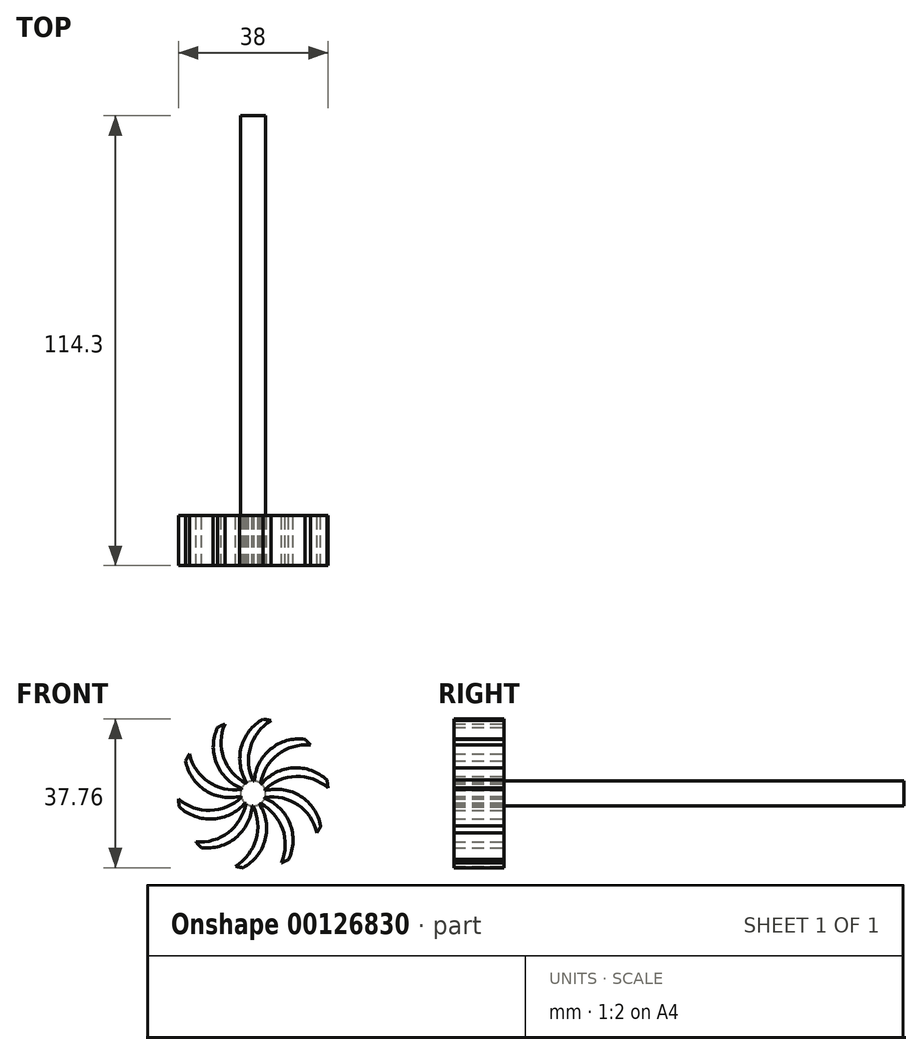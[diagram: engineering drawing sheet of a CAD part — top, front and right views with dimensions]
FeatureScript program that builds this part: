
annotation { "Feature Type Name" : "Feature", "Feature Type Description" : "" }
export const myFeature = defineFeature(function(context is Context, id is Id, definition is map)
    precondition{}
    {
        {
            var Q0;
            Q0=qCreatedBy(makeId("Front.planeOp"),FACE);
            var sketch = newSketch(context, id + "F0", { "sketchPlane" : qUnion([Q0])});
            skCircle(sketch, "E0", {"center": v(0, 0) * mm, "radius": 3.18 * mm});
            skSolve(sketch);
        }
        {
            var Q0;
            Q0=makeQuery(id+"F0.imprint","IMPRINT",FACE,{"disambiguationData":[TD([[makeQuery(id+"F0.imprint","IMPRINT",EDGE,{"derivedFrom":sQuery(id+"F0.wireOp",EDGE,"E0")}),1.0]])]});
            extrude(context, id + "F1", {"entities" : qUnion([Q0]), "depth" : 101.6 * mm});
        }
        {
            var Q0;
            Q0=makeQuery(id+"F1.opExtrude","CAP_FACE",FACE,{"disambiguationData":[OSD([sQuery(id+"F0.wireOp",EDGE,"E0")])],"isStart":false});
            var sketch = newSketch(context, id + "F2", { "sketchPlane" : qUnion([Q0])});
            skCircle(sketch, "E1", {"center": v(0, 0) * mm, "radius": 19.05 * mm});
            skArc(sketch, "E2", {"start": v(4.53, 18.5) * mm, "mid": v(-0.72, 11.72) * mm, "end": v(0, 3.18) * mm});
            skArc(sketch, "E3", {"start": v(2.56, 18.88) * mm, "mid": v(-3.04, 11.7) * mm, "end": v(-1.63, 2.72) * mm});
            skArc(sketch, "E4.1.0", {"start": v(-9.03, 16.77) * mm, "mid": v(-9.34, 7.69) * mm, "end": v(-2.92, 1.24) * mm});
            skArc(sketch, "E4.1.1", {"start": v(-7.2, 17.63) * mm, "mid": v(-7.47, 9.06) * mm, "end": v(-1.87, 2.57) * mm});
            skArc(sketch, "E4.2.0", {"start": v(-17.16, 8.26) * mm, "mid": v(-12.07, 0.73) * mm, "end": v(-3.1, -0.71) * mm});
            skArc(sketch, "E4.2.1", {"start": v(-16.2, 10.03) * mm, "mid": v(-11.37, 2.94) * mm, "end": v(-3.02, 0.98) * mm});
            skArc(sketch, "E4.3.0", {"start": v(-18.74, -3.4) * mm, "mid": v(-10.2, -6.5) * mm, "end": v(-2.09, -2.4) * mm});
            skArc(sketch, "E4.3.1", {"start": v(-19, -1.4) * mm, "mid": v(-10.93, -4.3) * mm, "end": v(-3.02, -0.98) * mm});
            skArc(sketch, "E4.4.0", {"start": v(-13.16, -13.77) * mm, "mid": v(-4.43, -11.26) * mm, "end": v(-0.28, -3.16) * mm});
            skArc(sketch, "E4.4.1", {"start": v(-14.54, -12.3) * mm, "mid": v(-6.3, -9.9) * mm, "end": v(-1.87, -2.57) * mm});
            skArc(sketch, "E4.5.0", {"start": v(-2.56, -18.88) * mm, "mid": v(3.04, -11.7) * mm, "end": v(1.63, -2.72) * mm});
            skArc(sketch, "E4.5.1", {"start": v(-4.53, -18.5) * mm, "mid": v(0.72, -11.72) * mm, "end": v(0, -3.17) * mm});
            skArc(sketch, "E4.6.0", {"start": v(9.03, -16.77) * mm, "mid": v(9.34, -7.69) * mm, "end": v(2.92, -1.24) * mm});
            skArc(sketch, "E4.6.1", {"start": v(7.2, -17.63) * mm, "mid": v(7.47, -9.06) * mm, "end": v(1.87, -2.57) * mm});
            skArc(sketch, "E4.7.0", {"start": v(17.16, -8.26) * mm, "mid": v(12.07, -0.73) * mm, "end": v(3.1, 0.71) * mm});
            skArc(sketch, "E4.7.1", {"start": v(16.2, -10.03) * mm, "mid": v(11.37, -2.94) * mm, "end": v(3.02, -0.98) * mm});
            skArc(sketch, "E4.8.0", {"start": v(18.74, 3.4) * mm, "mid": v(10.2, 6.5) * mm, "end": v(2.09, 2.4) * mm});
            skArc(sketch, "E4.8.1", {"start": v(19, 1.4) * mm, "mid": v(10.93, 4.3) * mm, "end": v(3.02, 0.98) * mm});
            skArc(sketch, "E4.9.0", {"start": v(13.16, 13.77) * mm, "mid": v(4.43, 11.26) * mm, "end": v(0.28, 3.16) * mm});
            skArc(sketch, "E4.9.1", {"start": v(14.54, 12.3) * mm, "mid": v(6.3, 9.9) * mm, "end": v(1.87, 2.57) * mm});
            skSolve(sketch);
        }
        {
            var Q0;
            {var subQ0=sQuery(id+"F2.wireOp",EDGE,"E2");Q0=makeQuery(id+"F2.imprint","IMPRINT",FACE,{"disambiguationData":[TD([[makeQuery(id+"F2.imprint","IMPRINT",EDGE,{"derivedFrom":subQ0}),-1.0]])]});}
            var Q1;
            {var subQ0=sQuery(id+"F2.wireOp",EDGE,"E4.9.0");Q1=makeQuery(id+"F2.imprint","IMPRINT",FACE,{"disambiguationData":[TD([[makeQuery(id+"F2.imprint","IMPRINT",EDGE,{"derivedFrom":subQ0}),1.0]])]});}
            var Q2;
            {var subQ0=sQuery(id+"F2.wireOp",EDGE,"E4.8.0");Q2=makeQuery(id+"F2.imprint","IMPRINT",FACE,{"disambiguationData":[TD([[makeQuery(id+"F2.imprint","IMPRINT",EDGE,{"derivedFrom":subQ0}),1.0]])]});}
            var Q3;
            {var subQ0=sQuery(id+"F2.wireOp",EDGE,"E4.7.0");Q3=makeQuery(id+"F2.imprint","IMPRINT",FACE,{"disambiguationData":[TD([[makeQuery(id+"F2.imprint","IMPRINT",EDGE,{"derivedFrom":subQ0}),1.0]])]});}
            var Q4;
            {var subQ0=sQuery(id+"F2.wireOp",EDGE,"E4.5.0");Q4=makeQuery(id+"F2.imprint","IMPRINT",FACE,{"disambiguationData":[TD([[makeQuery(id+"F2.imprint","IMPRINT",EDGE,{"derivedFrom":subQ0}),1.0]])]});}
            var Q5;
            {var subQ0=sQuery(id+"F2.wireOp",EDGE,"E4.6.0");Q5=makeQuery(id+"F2.imprint","IMPRINT",FACE,{"disambiguationData":[TD([[makeQuery(id+"F2.imprint","IMPRINT",EDGE,{"derivedFrom":subQ0}),1.0]])]});}
            var Q6;
            {var subQ0=sQuery(id+"F2.wireOp",EDGE,"E4.4.0");Q6=makeQuery(id+"F2.imprint","IMPRINT",FACE,{"disambiguationData":[TD([[makeQuery(id+"F2.imprint","IMPRINT",EDGE,{"derivedFrom":subQ0}),1.0]])]});}
            var Q7;
            {var subQ0=sQuery(id+"F2.wireOp",EDGE,"E4.3.0");Q7=makeQuery(id+"F2.imprint","IMPRINT",FACE,{"disambiguationData":[TD([[makeQuery(id+"F2.imprint","IMPRINT",EDGE,{"derivedFrom":subQ0}),1.0]])]});}
            var Q8;
            {var subQ0=sQuery(id+"F2.wireOp",EDGE,"E4.2.0");Q8=makeQuery(id+"F2.imprint","IMPRINT",FACE,{"disambiguationData":[TD([[makeQuery(id+"F2.imprint","IMPRINT",EDGE,{"derivedFrom":subQ0}),1.0]])]});}
            var Q9;
            {var subQ0=sQuery(id+"F2.wireOp",EDGE,"E4.1.0");Q9=makeQuery(id+"F2.imprint","IMPRINT",FACE,{"disambiguationData":[TD([[makeQuery(id+"F2.imprint","IMPRINT",EDGE,{"derivedFrom":subQ0}),1.0]])]});}
            var Q10;
            {var subQ0=makeQuery(id+"F1.opExtrude","CAP_EDGE",EDGE,{"disambiguationData":[OSD([sQuery(id+"F0.wireOp",EDGE,"E0")])],"isStart":false});var subQ9=makeQuery(id+"F2.imprint","INTERSECT",VERTEX,{"derivedFrom":[subQ0,sQuery(id+"F2.wireOp",EDGE,"E2")]});Q10=makeQuery(id+"F2.imprint","IMPRINT",FACE,{"disambiguationData":[TD([[makeQuery(id+"F2.imprint","IMPRINT",EDGE,{"disambiguationData":[TD([[subQ9,-1.0]])],"derivedFrom":subQ0}),1.0]])]});}
            extrude(context, id + "F3", {"entities" : qUnion([Q0, Q1, Q2, Q3, Q4, Q5, Q6, Q7, Q8, Q9, Q10]), "operationType" : NewBodyOperationType.ADD, "depth" : 12.7 * mm});
        }
    });
